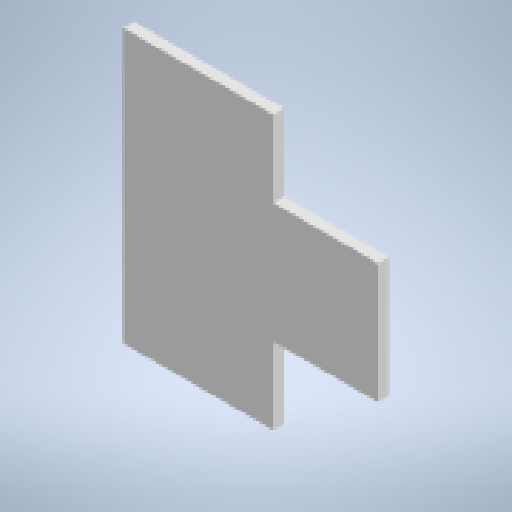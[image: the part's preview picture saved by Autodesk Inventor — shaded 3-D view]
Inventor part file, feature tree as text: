
AUTODESK INVENTOR PART (.ipt)
format: ipt  version: 2023 (Build 270158000, 158)  size: 139,776 bytes
history: native  units: in
note: dims shown in document units (in); Inventor stores cm internally (conversion verified against a paired STEP export)
features: other x8, reference x5, extrude x2, sketch x2, projected_geometry x1
ambient origin geometry x8: Origin, YZ Plane, XZ Plane, XY Plane, X Axis, Y Axis, Z Axis, Center Point
bodies: Body1 (feature_tree)
feature tree (18):
  other  "Bryła1"
  extrude  "Wyciągnięcie proste1"  Depth=0.0787in TaperAngle=0.0deg
  extrude  "Wyciągnięcie proste2"  TaperAngle=0.0deg  [1 undecoded]
  sketch  "Szkic1"
  reference  "Odniesienie1"
  reference  "Odniesienie2"
  reference  "Odniesienie3"
  reference  "Odniesienie4"
  sketch  "Szkic2"
  reference  "Odniesienie5"
  projected_geometry  "Pętla rzutowana1"
  other  "<userpath>\Documents\Inventor\MikroNalesnik\byk.iam"
  other  "byk.iam"
  other  "uchwyt silnikow:1"
  other  "spod:1"
  other  "wach:1"
  other  "wach:2"
  other  "nozzz:1"
note: 1 required parameter value undecoded (feature->parameter linkage not recoverable at this tier; creation-order binding heuristic only, values carry confidence <= 0.55)
